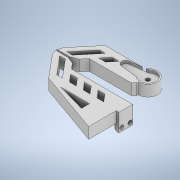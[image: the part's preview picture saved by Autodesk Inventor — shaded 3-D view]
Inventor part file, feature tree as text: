
AUTODESK INVENTOR PART (.ipt)
format: ipt  version: 2021 (Build 250183000, 183)  size: 347,648 bytes
history: native  units: mm
features: extrude x14, sketch x14, other x1, fillet x1, chamfer x1
ambient origin geometry x8: Origin, YZ Plane, XZ Plane, XY Plane, X Axis, Y Axis, Z Axis, Center Point
bodies: Body1 (feature_tree)
feature tree (31):
  other  "Sólido1"
  extrude  "Extrusión1"  Depth=6.0mm
  extrude  "Extrusión2"  Depth=8.0mm TaperAngle=0.0deg
  extrude  "Extrusión3"  Depth=4.0mm TaperAngle=0.0deg
  extrude  "Extrusión4"  Depth=8.0mm TaperAngle=0.0deg
  extrude  "Extrusión5"  Depth=2.0mm
  extrude  "Extrusión6"  Depth=2.0mm
  extrude  "Extrusión7"  Depth=3.0mm TaperAngle=0.0deg
  extrude  "Extrusión8"  Depth=5.0mm TaperAngle=0.0deg
  fillet  "Empalme1"  Radius=5.0mm
  chamfer  "Chaflán1"  Distance=5.0mm
  extrude  "Extrusión9"  Depth=5.0mm
  extrude  "Extrusión10"  Depth=10.0mm TaperAngle=0.0deg
  extrude  "Extrusión11"  Depth=10.0mm TaperAngle=0.0deg
  extrude  "Extrusión13"  Depth=8.0mm TaperAngle=0.0deg
  extrude  "Extrusión14"  Depth=2.0mm
  extrude  "Extrusión15"  Depth=2.0mm TaperAngle=45.0deg
  sketch  "Boceto1"  dims[d1=6.0mm d8=6.0mm]
  sketch  "Boceto2"  dims[d9=0.5mm d10=8.0mm d11=0.0mm]
  sketch  "Boceto3"  dims[d12=6.0mm d13=4.0mm d14=0.0mm]
  sketch  "Boceto4"  dims[d15=5.0mm d16=8.0mm d17=0.0mm]
  sketch  "Boceto5"  dims[d18=5.0mm d19=2.0mm]
  sketch  "Boceto6"  dims[d20=2.0mm d21=3.0mm]
  sketch  "Boceto7"  dims[d22=3.0mm d23=3.0mm d24=0.0mm]
  sketch  "Boceto8"  dims[d25=3.0mm d26=5.0mm d27=0.0mm d28=5.0mm]
  sketch  "Boceto9"  dims[d29=5.0mm]
  sketch  "Boceto10"  dims[d30=5.0mm]
  sketch  "Boceto12"  dims[d31=5.0mm]
  sketch  "Boceto14"  dims[d32=5.0mm]
  sketch  "Boceto15"  dims[d33=5.0mm]
  sketch  "Boceto16"  dims[d34=5.0mm d35=5.0mm d36=5.0mm d37=10.0mm d38=0.0mm d39=10.0mm d40=0.0mm d41=8.0mm d42=0.0mm d43=2.0mm d44=2.0mm d45=2.0mm d46=45.0deg d47=6.0mm d48=4.0mm d49=0.0mm d50=12.0mm d51=19.0mm d52=4.5mm d53=9.0mm d54=3.0mm d55=2.0mm d56=0.0mm d57=2.0mm d58=20.0mm d59=5.0mm d60=5.0mm d61=5.0mm d62=8.0mm d63=0.0mm d64=5.0mm d68=8.0mm d69=0.0mm d70=8.0mm d71=0.0mm d72=5.0mm d73=5.0mm d74=5.0mm d75=5.0mm d76=5.0mm d77=5.0mm d78=5.0mm d79=5.0mm d80=8.0mm d81=0.0mm]
